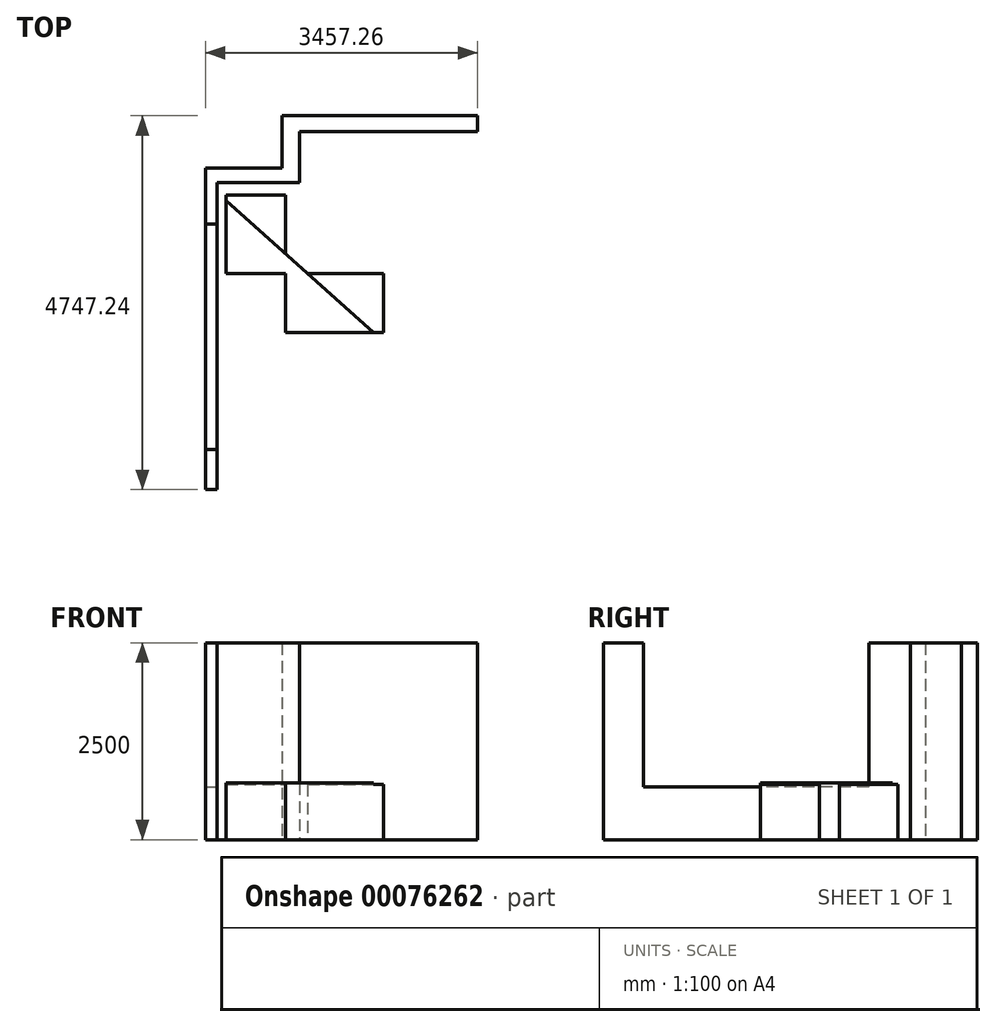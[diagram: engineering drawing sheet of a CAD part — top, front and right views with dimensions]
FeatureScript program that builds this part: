
annotation { "Feature Type Name" : "Feature", "Feature Type Description" : "" }
export const myFeature = defineFeature(function(context is Context, id is Id, definition is map)
    precondition{}
    {
        {
            var Q0;
            Q0=qCreatedBy(makeId("Top.planeOp"),FACE);
            var sketch = newSketch(context, id + "F0", { "sketchPlane" : qUnion([Q0])});
            skLineSegment(sketch, "E0", {"start": v(0, 0) * mm, "end": v(0, 3900) * mm});
            skLineSegment(sketch, "E1", {"start": v(0, 3900) * mm, "end": v(1050, 3900) * mm});
            skLineSegment(sketch, "E2", {"start": v(1050, 3900) * mm, "end": v(1050, 4545) * mm});
            skLineSegment(sketch, "E3", {"start": v(1050, 4545) * mm, "end": v(3310, 4545) * mm});
            skLineSegment(sketch, "E4", {"start": v(3310, 4545) * mm, "end": v(3310, 4747.24) * mm});
            skLineSegment(sketch, "E5", {"start": v(3310, 4747.24) * mm, "end": v(825.86, 4747.24) * mm});
            skLineSegment(sketch, "E6", {"start": v(825.86, 4747.24) * mm, "end": v(825.86, 4085.52) * mm});
            skLineSegment(sketch, "E7", {"start": v(825.86, 4085.52) * mm, "end": v(-147.26, 4085.52) * mm});
            skLineSegment(sketch, "E8", {"start": v(-147.26, 4085.52) * mm, "end": v(-147.26, 0) * mm});
            skLineSegment(sketch, "E9", {"start": v(-147.26, 0) * mm, "end": v(0, 0) * mm});
            skSolve(sketch);
        }
        {
            var Q0;
            Q0=makeQuery(id+"F0.imprint","IMPRINT",FACE,{"disambiguationData":[TD([[makeQuery(id+"F0.imprint","IMPRINT",EDGE,{"derivedFrom":sQuery(id+"F0.wireOp",EDGE,"E0")}),1.0]])]});
            extrude(context, id + "F1", {"entities" : qUnion([Q0]), "depth" : 2500 * mm});
        }
        {
            var Q0;
            Q0=makeQuery(id+"F1.opExtrude","SWEPT_FACE",FACE,{"disambiguationData":[OSD([sQuery(id+"F0.wireOp",EDGE,"E0")])]});
            var sketch = newSketch(context, id + "F2", { "sketchPlane" : qUnion([Q0])});
            skLineSegment(sketch, "E10.bottom", {"start": v(3370, 670) * mm, "end": v(510, 670) * mm});
            skLineSegment(sketch, "E10.top", {"start": v(3370, 2500) * mm, "end": v(510, 2500) * mm});
            skLineSegment(sketch, "E10.left", {"start": v(3370, 670) * mm, "end": v(3370, 2500) * mm});
            skLineSegment(sketch, "E10.right", {"start": v(510, 670) * mm, "end": v(510, 2500) * mm});
            skSolve(sketch);
        }
        {
            var Q0;
            Q0=makeQuery(id+"F2.imprint","IMPRINT",FACE,{"disambiguationData":[TD([[makeQuery(id+"F2.imprint","IMPRINT",EDGE,{"derivedFrom":sQuery(id+"F2.wireOp",EDGE,"E10.bottom")}),-1.0]])]});
            extrude(context, id + "F3", {"entities" : qUnion([Q0]), "operationType" : NewBodyOperationType.REMOVE, "oppositeDirection" : true, "depth" : 200 * mm});
        }
        {
            var Q0;
            Q0=qCreatedBy(makeId("Top.planeOp"),FACE);
            var sketch = newSketch(context, id + "F4", { "sketchPlane" : qUnion([Q0])});
            skLineSegment(sketch, "E11.bottom", {"start": v(867.94, 3742.13) * mm, "end": v(117.94, 3742.13) * mm});
            skLineSegment(sketch, "E11.top", {"start": v(867.94, 1992.13) * mm, "end": v(117.94, 1992.13) * mm});
            skLineSegment(sketch, "E11.left", {"start": v(867.94, 3742.13) * mm, "end": v(867.94, 1992.13) * mm});
            skLineSegment(sketch, "E11.right", {"start": v(117.94, 3742.13) * mm, "end": v(117.94, 1992.13) * mm});
            skLineSegment(sketch, "E12.bottom", {"start": v(2117.94, 1992.13) * mm, "end": v(117.94, 1992.13) * mm});
            skLineSegment(sketch, "E12.top", {"start": v(2117.94, 2742.13) * mm, "end": v(117.94, 2742.13) * mm});
            skLineSegment(sketch, "E12.left", {"start": v(2117.94, 1992.13) * mm, "end": v(2117.94, 2742.13) * mm});
            skLineSegment(sketch, "E12.right", {"start": v(117.94, 1992.13) * mm, "end": v(117.94, 2742.13) * mm});
            skLineSegment(sketch, "E13", {"start": v(117.94, 3668.11) * mm, "end": v(1987.13, 1992.13) * mm});
            skSolve(sketch);
        }
        {
            var Q0;
            {var subQ0=sQuery(id+"F4.wireOp",EDGE,"E12.bottom");var subQ1=sQuery(id+"F4.wireOp",EDGE,"E11.left");var subQ2=makeQuery(id+"F4.imprint","INTERSECT",VERTEX,{"derivedFrom":[subQ1,subQ0]});Q0=makeQuery(id+"F4.imprint","IMPRINT",FACE,{"disambiguationData":[TD([[makeQuery(id+"F4.imprint","IMPRINT",EDGE,{"disambiguationData":[TD([[subQ2,1.0]])],"derivedFrom":subQ1}),1.0]])]});}
            var Q1;
            {var subQ0=sQuery(id+"F4.wireOp",EDGE,"E13");var subQ1=sQuery(id+"F4.wireOp",EDGE,"E11.left");var subQ2=makeQuery(id+"F4.imprint","INTERSECT",VERTEX,{"derivedFrom":[subQ1,subQ0]});Q1=makeQuery(id+"F4.imprint","IMPRINT",FACE,{"disambiguationData":[TD([[makeQuery(id+"F4.imprint","IMPRINT",EDGE,{"disambiguationData":[TD([[subQ2,-1.0]])],"derivedFrom":subQ1}),1.0]])]});}
            var Q2;
            {var subQ0=sQuery(id+"F4.wireOp",EDGE,"E13");var subQ1=sQuery(id+"F4.wireOp",EDGE,"E11.left");var subQ2=makeQuery(id+"F4.imprint","INTERSECT",VERTEX,{"derivedFrom":[subQ1,subQ0]});Q2=makeQuery(id+"F4.imprint","IMPRINT",FACE,{"disambiguationData":[TD([[makeQuery(id+"F4.imprint","IMPRINT",EDGE,{"disambiguationData":[TD([[subQ2,-1.0]])],"derivedFrom":subQ1}),-1.0]])]});}
            var Q3;
            {var subQ5=sQuery(id+"F4.wireOp",EDGE,"E12.right");Q3=makeQuery(id+"F4.imprint","IMPRINT",FACE,{"disambiguationData":[TD([[makeQuery(id+"F4.imprint","IMPRINT",EDGE,{"derivedFrom":subQ5}),-1.0]])]});}
            extrude(context, id + "F5", {"entities" : qUnion([Q0, Q1, Q2, Q3]), "depth" : 720 * mm});
        }
        {
            var Q0;
            {var subQ0=sQuery(id+"F4.wireOp",EDGE,"E11.bottom");Q0=makeQuery(id+"F4.imprint","IMPRINT",FACE,{"disambiguationData":[TD([[makeQuery(id+"F4.imprint","IMPRINT",EDGE,{"derivedFrom":subQ0}),1.0]])]});}
            var Q1;
            {var subQ0=sQuery(id+"F4.wireOp",EDGE,"E12.left");Q1=makeQuery(id+"F4.imprint","IMPRINT",FACE,{"disambiguationData":[TD([[makeQuery(id+"F4.imprint","IMPRINT",EDGE,{"derivedFrom":subQ0}),1.0]])]});}
            extrude(context, id + "F6", {"entities" : qUnion([Q0, Q1]), "operationType" : NewBodyOperationType.ADD, "depth" : 700 * mm});
        }
    });
